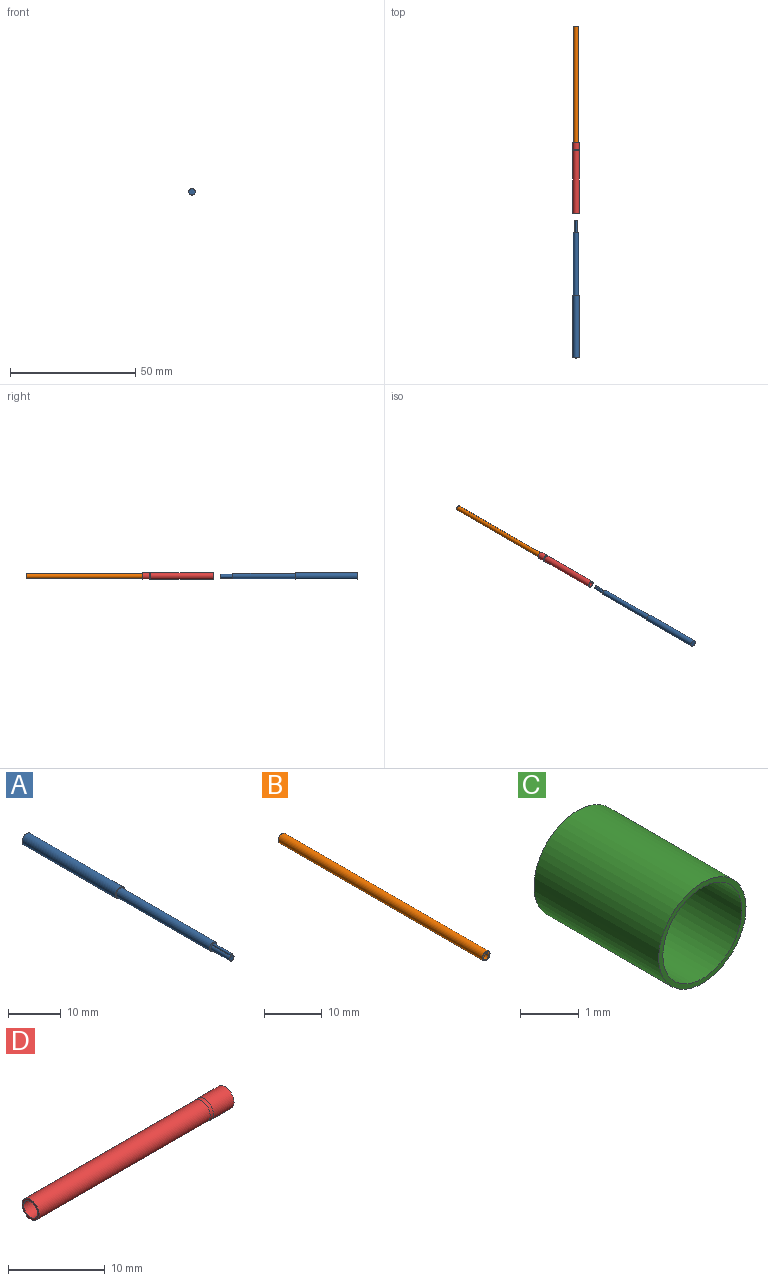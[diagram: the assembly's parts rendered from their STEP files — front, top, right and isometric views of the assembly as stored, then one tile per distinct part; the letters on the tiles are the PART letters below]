
ASSEMBLY  parts=4 mates=3
PART A: 8 faces, bbox 2.5x55x2.5 mm
  f0: cylinder r=0.6mm len=5mm, axis (0,1,0), area 17.1mm2, adj f1,f2,f4
  f1: cylinder r=0.25mm len=5mm, axis (0,1,0), area 5.9mm2, adj f0,f2,f4
  f2: plane 1.6x1.2mm, normal (0,-1,0), area 1.3mm2, adj f0,f1
  f3: cylinder r=1mm len=25mm, axis (0,-1,0), area 157.1mm2, adj f4,f7
  f4: plane 2x2mm, normal (0,-1,0), area 1.8mm2, adj f0,f1,f3
  f5: cylinder r=1.25mm len=25mm, axis (0,-1,0), area 196.3mm2, adj f6,f7
  f6: plane 2.5x2.5mm, normal (0,1,0), area 4.9mm2, adj f5
  f7: plane 2.5x2.5mm, normal (0,-1,0), area 1.8mm2, adj f3,f5
PART B: 5 faces, bbox 1.9x50x1.9 mm
  f0: cylinder r=0.25mm len=50mm, axis (0,1,0), area 58.9mm2, adj f1,f3,f4
  f1: cylinder r=0.6mm len=50mm, axis (0,1,0), area 170.5mm2, adj f0,f3,f4
  f2: cylinder r=0.95mm len=50mm, axis (0,1,0), area 298.5mm2, adj f3,f4
  f3: plane 1.9x1.9mm, normal (0,-1,0), area 1.5mm2, adj f0,f1,f2
  f4: plane 1.9x1.9mm, normal (0,1,0), area 1.5mm2, adj f0,f1,f2
PART C: 4 faces, bbox 2.1x3x2.1 mm
  f0: cylinder r=0.95mm len=3mm, axis (0,1,0), area 17.9mm2, adj f2,f3
  f1: cylinder r=1.05mm len=3mm, axis (0,1,0), area 19.8mm2, adj f2,f3
  f2: plane 2.1x2.1mm, normal (0,-1,0), area 0.6mm2, adj f0,f1
  f3: plane 2.1x2.1mm, normal (0,1,0), area 0.6mm2, adj f0,f1
PART D: 8 faces, bbox 28.4x2.6x2.6 mm
  f0: plane 2.5x2.5mm, normal (-1,0,0), area 1.8mm2, adj f1,f7
  f1: cylinder r=1mm len=25mm, axis (-1,0,0), area 157.1mm2, adj f0,f2
  f2: cone r=1mm half-angle=6.6deg, axis (1,0,0), area 2.8mm2, adj f1,f3
  f3: cylinder r=1.05mm len=3mm, axis (-1,0,0), area 19.8mm2, adj f2,f4
  f4: plane 2.6x2.6mm, normal (1,0,0), area 1.8mm2, adj f3,f5
  f5: cylinder r=1.3mm len=3mm, axis (-1,0,0), area 24.5mm2, adj f4,f6
  f6: cone r=1.3mm half-angle=6.6deg, axis (1,0,0), area 3.5mm2, adj f5,f7
  f7: cylinder r=1.25mm len=25mm, axis (-1,0,0), area 196.3mm2, adj f0,f6
PLACE A rot(axis=(0,0,1),180deg) t=(-10.87,-64.66,-4.03)mm
PLACE B rot(axis=(0,0,1),180deg) t=(-10.87,-32.03,-4.03)mm
PLACE C rot(axis=(0.71,0,-0.71),180deg) t=(-10.87,-31.41,-4.03)mm
PLACE D rot(axis=(0,0,1),90deg) t=(-10.87,-33.98,-4.03)mm
MATE slider A.f5 <-> D.f1  axis (0,1,0) through (-10.87,-102.16,-4.03)mm
MATE slider D.f1 <-> B.f2  axis (0,-1,0) through (-10.87,-44.36,-4.03)mm
MATE slider B.f2 <-> C.f0  axis (0,-1,0) through (-10.87,-7.03,-4.03)mm
